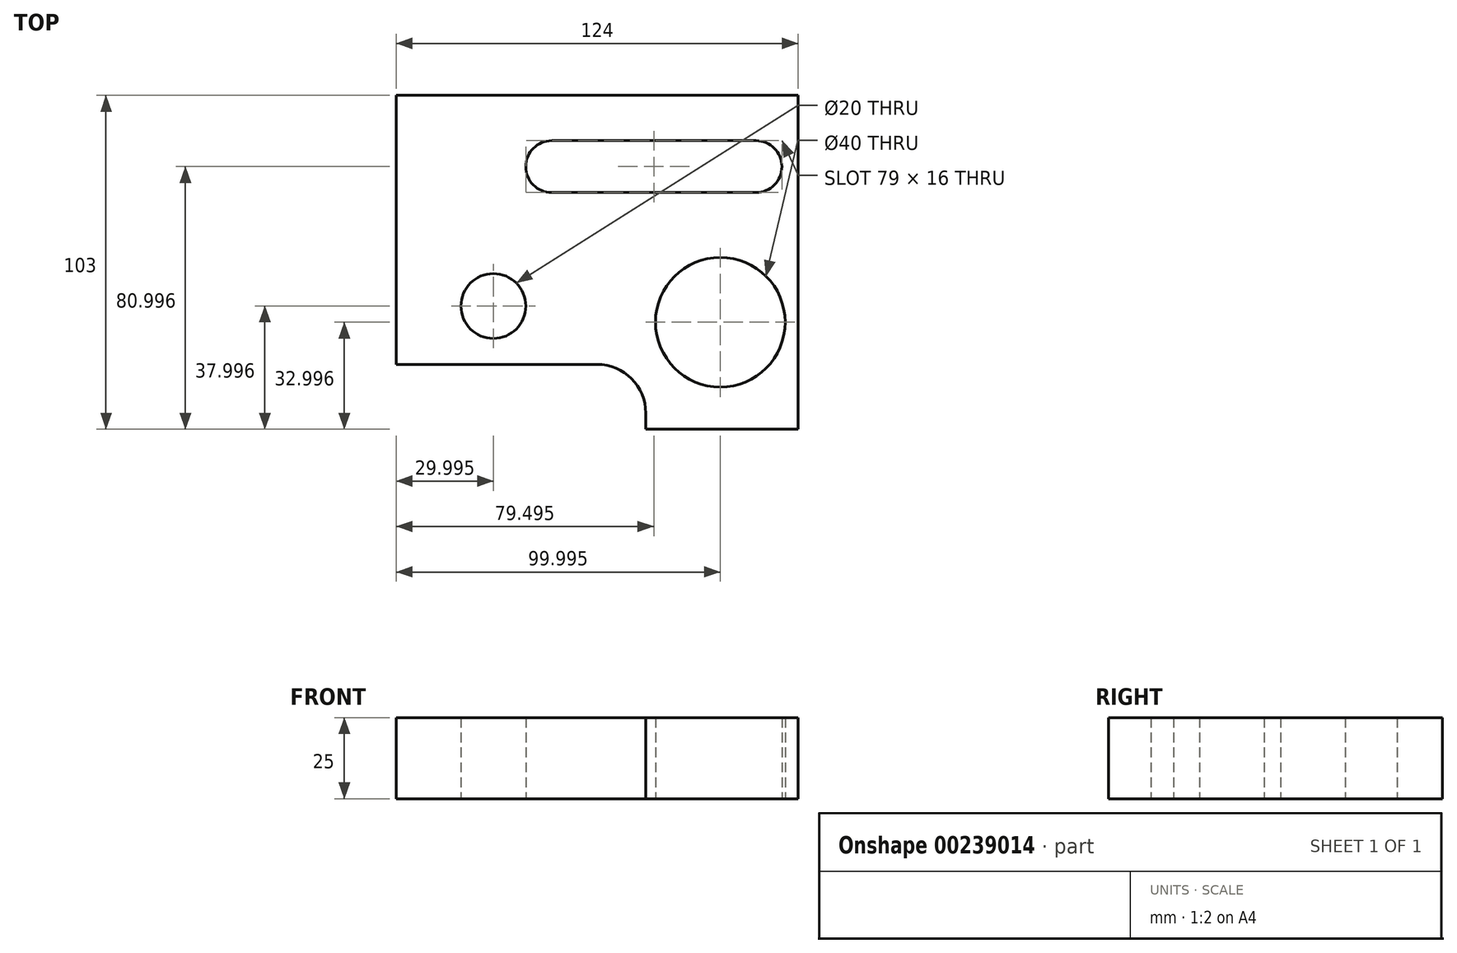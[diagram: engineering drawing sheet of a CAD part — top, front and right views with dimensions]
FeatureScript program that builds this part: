
annotation { "Feature Type Name" : "Feature", "Feature Type Description" : "" }
export const myFeature = defineFeature(function(context is Context, id is Id, definition is map)
    precondition{}
    {
        {
            var Q0;
            Q0=qCreatedBy(makeId("Top.planeOp"),FACE);
            var sketch = newSketch(context, id + "F0", { "sketchPlane" : qUnion([Q0])});
            skLineSegment(sketch, "E0", {"start": v(-66.42, 37.27) * mm, "end": v(-66.42, -45.73) * mm});
            skLineSegment(sketch, "E1", {"start": v(-66.42, 37.27) * mm, "end": v(57.58, 37.27) * mm});
            skLineSegment(sketch, "E2", {"start": v(57.58, 37.27) * mm, "end": v(57.58, -65.73) * mm});
            skLineSegment(sketch, "E3", {"start": v(57.58, -65.73) * mm, "end": v(10.58, -65.73) * mm});
            skLineSegment(sketch, "E4", {"start": v(10.58, -65.73) * mm, "end": v(10.58, -60.73) * mm});
            skLineSegment(sketch, "E5", {"start": v(-4.42, -45.73) * mm, "end": v(-66.42, -45.73) * mm});
            skLineSegment(sketch, "E6", {"start": v(44.58, 23.27) * mm, "end": v(-18.42, 23.27) * mm});
            skLineSegment(sketch, "E7", {"start": v(-26.42, 15.27) * mm, "end": v(-26.42, 15.27) * mm});
            skLineSegment(sketch, "E8", {"start": v(-18.42, 7.27) * mm, "end": v(44.58, 7.27) * mm});
            skLineSegment(sketch, "E9", {"start": v(52.58, 15.27) * mm, "end": v(52.58, 15.27) * mm});
            skPoint(sketch, "E10.end.orphan", {"position": v(52.58, 37.27) * mm});
            skPoint(sketch, "E11.visualSharp", {"position": v(-26.42, 23.27) * mm});
            skArc(sketch, "E11.filletArc", {"start": v(-18.42, 23.27) * mm, "mid": v(-24.08, 20.92) * mm, "end": v(-26.42, 15.27) * mm});
            skPoint(sketch, "E12.visualSharp", {"position": v(-26.42, 7.27) * mm});
            skArc(sketch, "E12.filletArc", {"start": v(-26.42, 15.27) * mm, "mid": v(-24.08, 9.6) * mm, "end": v(-18.42, 7.27) * mm});
            skPoint(sketch, "E13.visualSharp", {"position": v(52.58, 7.27) * mm});
            skArc(sketch, "E13.filletArc", {"start": v(44.58, 7.27) * mm, "mid": v(50.23, 9.6) * mm, "end": v(52.58, 15.27) * mm});
            skPoint(sketch, "E14.visualSharp", {"position": v(52.58, 23.27) * mm});
            skArc(sketch, "E14.filletArc", {"start": v(52.58, 15.27) * mm, "mid": v(50.23, 20.92) * mm, "end": v(44.58, 23.27) * mm});
            skLineSegment(sketch, "E15", {"start": v(-66.42, 37.27) * mm, "end": v(-76.42, 37.27) * mm});
            skCircle(sketch, "E16", {"center": v(-36.42, -27.73) * mm, "radius": 10 * mm});
            skCircle(sketch, "E17", {"center": v(33.58, -32.73) * mm, "radius": 20 * mm});
            skPoint(sketch, "E18.visualSharp", {"position": v(10.58, -45.73) * mm});
            skArc(sketch, "E18.filletArc", {"start": v(10.58, -60.73) * mm, "mid": v(6.18, -50.13) * mm, "end": v(-4.42, -45.73) * mm});
            skSolve(sketch);
        }
        {
            var Q0;
            Q0=makeQuery(id+"F0.imprint","IMPRINT",FACE,{"disambiguationData":[TD([[makeQuery(id+"F0.imprint","IMPRINT",EDGE,{"derivedFrom":sQuery(id+"F0.wireOp",EDGE,"E0")}),1.0]])]});
            extrude(context, id + "F1", {"entities" : qUnion([Q0]), "depth" : 25 * mm});
        }
    });
